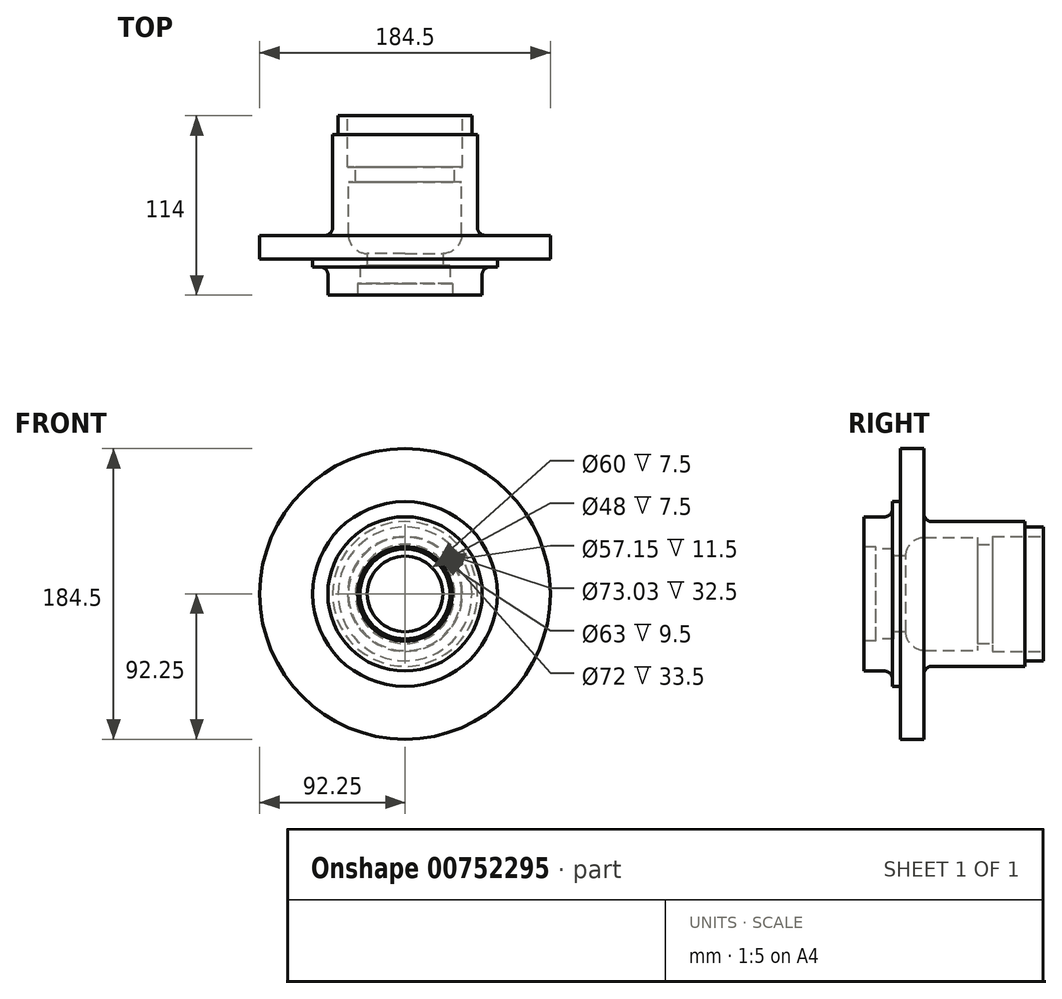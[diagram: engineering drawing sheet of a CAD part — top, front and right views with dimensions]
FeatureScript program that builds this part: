
annotation { "Feature Type Name" : "Feature", "Feature Type Description" : "" }
export const myFeature = defineFeature(function(context is Context, id is Id, definition is map)
    precondition{}
    {
        {
            var Q0;
            Q0=qCreatedBy(makeId("Front.planeOp"),FACE);
            var sketch = newSketch(context, id + "F0", { "sketchPlane" : qUnion([Q0])});
            skCircle(sketch, "E0", {"center": v(0, 0) * mm, "radius": 92.25 * mm});
            skSolve(sketch);
        }
        {
            var Q0;
            Q0 = qSketchRegion(id + "F0", true);
            extrude(context, id + "F1", {"entities" : qUnion([Q0]), "depth" : 114 * mm, "offsetDistance" : 25 * mm});
        }
        {
            var Q0;
            Q0=makeQuery(id+"F1.opExtrude","CAP_FACE",FACE,{"disambiguationData":[OSD([sQuery(id+"F0.wireOp",EDGE,"E0")])],"isStart":false});
            var sketch = newSketch(context, id + "F2", { "sketchPlane" : qUnion([Q0])});
            skCircle(sketch, "E1", {"center": v(0, 0) * mm, "radius": 92.25 * mm});
            skCircle(sketch, "E2", {"center": v(0, 0) * mm, "radius": 49 * mm});
            skSolve(sketch);
        }
        {
            var Q0;
            Q0 = qSketchRegion(id + "F2", true);
            extrude(context, id + "F3", {"entities" : qUnion([Q0]), "operationType" : NewBodyOperationType.REMOVE, "oppositeDirection" : true, "depth" : 18 * mm, "offsetDistance" : 25 * mm});
        }
        {
            var Q0;
            Q0=makeQuery(id+"F3.boolean.opBoolean","COPY",EDGE,{"derivedFrom":makeQuery(id+"F3.opExtrude","CAP_EDGE",EDGE,{"disambiguationData":[OSD([sQuery(id+"F2.wireOp",EDGE,"E2")])],"isStart":false})});
            fillet(context, id + "F4", {"entities" : qUnion([Q0]), "radius" : 5 * mm, "tangentPropagation" : true, "allowEdgeOverflow" : false});
        }
        {
            var Q0;
            Q0=makeQuery(id+"F1.opExtrude","CAP_FACE",FACE,{"disambiguationData":[OSD([sQuery(id+"F0.wireOp",EDGE,"E0")])],"isStart":false});
            var sketch = newSketch(context, id + "F5", { "sketchPlane" : qUnion([Q0])});
            skCircle(sketch, "E3", {"center": v(0, 0) * mm, "radius": 24 * mm});
            skSolve(sketch);
        }
        {
            var Q0;
            Q0=makeQuery(id+"F5.imprint","IMPRINT",FACE,{"disambiguationData":[TD([[makeQuery(id+"F5.imprint","IMPRINT",EDGE,{"derivedFrom":sQuery(id+"F5.wireOp",EDGE,"E3")}),1.0]])]});
            extrude(context, id + "F6", {"entities" : qUnion([Q0]), "operationType" : NewBodyOperationType.REMOVE, "oppositeDirection" : true, "depth" : 26.5 * mm, "offsetDistance" : 25 * mm});
        }
        {
            var Q0;
            Q0=makeQuery(id+"F1.opExtrude","CAP_FACE",FACE,{"disambiguationData":[OSD([sQuery(id+"F0.wireOp",EDGE,"E0")])],"isStart":false});
            var sketch = newSketch(context, id + "F7", { "sketchPlane" : qUnion([Q0])});
            skCircle(sketch, "E4", {"center": v(0, 0) * mm, "radius": 28.57 * mm});
            skSolve(sketch);
        }
        {
            var Q0;
            Q0 = qSketchRegion(id + "F7", true);
            extrude(context, id + "F8", {"entities" : qUnion([Q0]), "operationType" : NewBodyOperationType.REMOVE, "oppositeDirection" : true, "depth" : 19 * mm, "offsetDistance" : 25 * mm});
        }
        {
            var Q0;
            Q0=makeQuery(id+"F1.opExtrude","CAP_FACE",FACE,{"disambiguationData":[OSD([sQuery(id+"F0.wireOp",EDGE,"E0")])],"isStart":false});
            var sketch = newSketch(context, id + "F9", { "sketchPlane" : qUnion([Q0])});
            skCircle(sketch, "E5", {"center": v(0, 0) * mm, "radius": 30 * mm});
            skSolve(sketch);
        }
        {
            var Q0;
            Q0 = qSketchRegion(id + "F9", true);
            extrude(context, id + "F10", {"entities" : qUnion([Q0]), "operationType" : NewBodyOperationType.REMOVE, "oppositeDirection" : true, "depth" : 7.5 * mm, "offsetDistance" : 25 * mm});
        }
        {
            var Q0;
            Q0=makeQuery(id+"F1.opExtrude","CAP_FACE",FACE,{"disambiguationData":[OSD([sQuery(id+"F0.wireOp",EDGE,"E0")])],"isStart":true});
            var sketch = newSketch(context, id + "F11", { "sketchPlane" : qUnion([Q0])});
            skCircle(sketch, "E6", {"center": v(0, 0) * mm, "radius": 46 * mm});
            skSolve(sketch);
        }
        {
            var Q0;
            Q0=makeQuery(id+"F11.imprint","IMPRINT",FACE,{"disambiguationData":[TD([[makeQuery(id+"F11.imprint","IMPRINT",EDGE,{"derivedFrom":sQuery(id+"F11.wireOp",EDGE,"E6")}),-1.0]])]});
            extrude(context, id + "F12", {"entities" : qUnion([Q0]), "operationType" : NewBodyOperationType.REMOVE, "oppositeDirection" : true, "depth" : 76 * mm, "offsetDistance" : 25 * mm});
        }
        {
            var Q0;
            Q0=makeQuery(id+"F1.opExtrude","CAP_FACE",FACE,{"disambiguationData":[OSD([sQuery(id+"F0.wireOp",EDGE,"E0")])],"isStart":true});
            var sketch = newSketch(context, id + "F13", { "sketchPlane" : qUnion([Q0])});
            skCircle(sketch, "E7", {"center": v(0, 0) * mm, "radius": 42.5 * mm});
            skCircle(sketch, "E8", {"center": v(0, 0) * mm, "radius": 46 * mm});
            skSolve(sketch);
        }
        {
            var Q0;
            Q0 = qSketchRegion(id + "F13", true);
            extrude(context, id + "F14", {"entities" : qUnion([Q0]), "operationType" : NewBodyOperationType.REMOVE, "oppositeDirection" : true, "depth" : 12 * mm, "offsetDistance" : 25 * mm});
        }
        {
            var Q0;
            Q0=makeQuery(id+"F1.opExtrude","CAP_FACE",FACE,{"disambiguationData":[OSD([sQuery(id+"F0.wireOp",EDGE,"E0")])],"isStart":true});
            var sketch = newSketch(context, id + "F15", { "sketchPlane" : qUnion([Q0])});
            skCircle(sketch, "E9", {"center": v(0, 0) * mm, "radius": 31.5 * mm});
            skSolve(sketch);
        }
        {
            var Q0;
            Q0 = qSketchRegion(id + "F15", true);
            extrude(context, id + "F16", {"entities" : qUnion([Q0]), "operationType" : NewBodyOperationType.REMOVE, "oppositeDirection" : true, "depth" : 42 * mm, "offsetDistance" : 25 * mm});
        }
        {
            var Q0;
            Q0=makeQuery(id+"F1.opExtrude","CAP_FACE",FACE,{"disambiguationData":[OSD([sQuery(id+"F0.wireOp",EDGE,"E0")])],"isStart":true});
            var sketch = newSketch(context, id + "F17", { "sketchPlane" : qUnion([Q0])});
            skCircle(sketch, "E10", {"center": v(0, 0) * mm, "radius": 36.51 * mm});
            skSolve(sketch);
        }
        {
            var Q0;
            Q0 = qSketchRegion(id + "F17", true);
            extrude(context, id + "F18", {"entities" : qUnion([Q0]), "operationType" : NewBodyOperationType.REMOVE, "oppositeDirection" : true, "depth" : 32.5 * mm, "offsetDistance" : 25 * mm});
        }
        {
            var Q0;
            Q0=makeQuery(id+"F16.boolean.opBoolean","COPY",FACE,{"derivedFrom":makeQuery(id+"F16.opExtrude","CAP_FACE",FACE,{"disambiguationData":[OSD([sQuery(id+"F15.wireOp",EDGE,"E9")])],"isStart":false})});
            var sketch = newSketch(context, id + "F19", { "sketchPlane" : qUnion([Q0])});
            skCircle(sketch, "E11", {"center": v(0, 0) * mm, "radius": 36 * mm});
            skSolve(sketch);
        }
        {
            var Q0;
            Q0 = qSketchRegion(id + "F19", true);
            extrude(context, id + "F20", {"entities" : qUnion([Q0]), "operationType" : NewBodyOperationType.REMOVE, "oppositeDirection" : true, "depth" : 45.5 * mm, "offsetDistance" : 25 * mm});
        }
        {
            var Q0;
            Q0=makeQuery(id+"F20.boolean.opBoolean","COPY",EDGE,{"derivedFrom":makeQuery(id+"F20.opExtrude","CAP_EDGE",EDGE,{"disambiguationData":[OSD([sQuery(id+"F19.wireOp",EDGE,"E11")])],"isStart":false})});
            fillet(context, id + "F21", {"entities" : qUnion([Q0]), "radius" : 12 * mm, "tangentPropagation" : true, "allowEdgeOverflow" : false});
        }
        {
            var Q0;
            Q0=makeQuery(id+"F12.boolean.opBoolean","COPY",EDGE,{"derivedFrom":makeQuery(id+"F12.opExtrude","CAP_EDGE",EDGE,{"disambiguationData":[OSD([sQuery(id+"F11.wireOp",EDGE,"E6")])],"isStart":false})});
            fillet(context, id + "F22", {"entities" : qUnion([Q0]), "radius" : 5 * mm, "tangentPropagation" : true, "allowEdgeOverflow" : false});
        }
        {
            var Q0;
            Q0=makeQuery(id+"F1.opExtrude","CAP_FACE",FACE,{"disambiguationData":[OSD([sQuery(id+"F0.wireOp",EDGE,"E0")])],"isStart":false});
            var sketch = newSketch(context, id + "F23", { "sketchPlane" : qUnion([Q0])});
            skCircle(sketch, "E12", {"center": v(0, 0) * mm, "radius": 92.75 * mm});
            skCircle(sketch, "E13", {"center": v(0, 0) * mm, "radius": 58.66 * mm});
            skSolve(sketch);
        }
        {
            var Q0;
            Q0=makeQuery(id+"F23.imprint","IMPRINT",FACE,{"disambiguationData":[TD([[makeQuery(id+"F23.imprint","IMPRINT",EDGE,{"derivedFrom":sQuery(id+"F23.wireOp",EDGE,"E12")}),1.0]])]});
            extrude(context, id + "F24", {"entities" : qUnion([Q0]), "operationType" : NewBodyOperationType.REMOVE, "oppositeDirection" : true, "depth" : 23 * mm, "offsetDistance" : 25 * mm});
        }
    });
